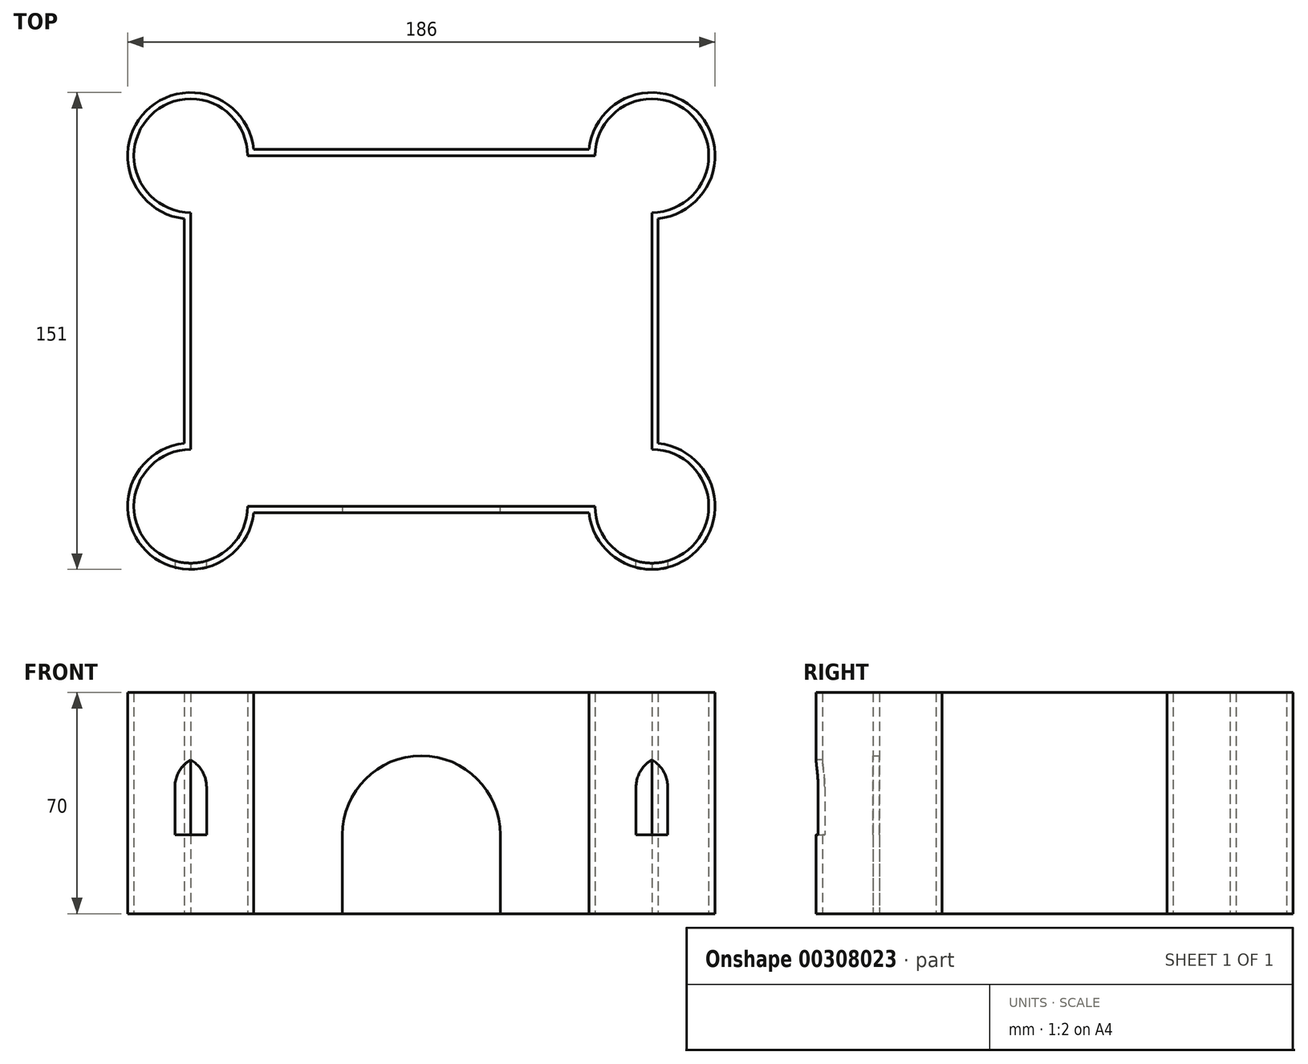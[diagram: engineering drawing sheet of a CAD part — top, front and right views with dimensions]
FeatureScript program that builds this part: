
annotation { "Feature Type Name" : "Feature", "Feature Type Description" : "" }
export const myFeature = defineFeature(function(context is Context, id is Id, definition is map)
    precondition{}
    {
        {
            var Q0;
            Q0=qCreatedBy(makeId("Top.planeOp"),FACE);
            var sketch = newSketch(context, id + "F0", { "sketchPlane" : qUnion([Q0])});
            skLineSegment(sketch, "E0.top", {"start": v(-53.1, 57.5) * mm, "end": v(53.1, 57.5) * mm});
            skLineSegment(sketch, "E0.left", {"start": v(-75, -35.6) * mm, "end": v(-75, 35.6) * mm});
            skPoint(sketch, "E0.middle", {"position": v(0, 0) * mm});
            skLineSegment(sketch, "E1.bottom", {"start": v(55, -55.5) * mm, "end": v(-55, -55.5) * mm});
            skLineSegment(sketch, "E1.top", {"start": v(55, 55.5) * mm, "end": v(-55, 55.5) * mm});
            skLineSegment(sketch, "E1.left", {"start": v(73, -37.5) * mm, "end": v(73, 37.5) * mm});
            skLineSegment(sketch, "E1.right", {"start": v(-73, -37.5) * mm, "end": v(-73, 37.5) * mm});
            skArc(sketch, "E2", {"start": v(-75, -35.6) * mm, "mid": v(-87.14, -69.64) * mm, "end": v(-53.1, -57.5) * mm});
            skArc(sketch, "E3", {"start": v(-73, -37.5) * mm, "mid": v(-85.73, -68.23) * mm, "end": v(-55, -55.5) * mm});
            skArc(sketch, "E4.MirrorC", {"start": v(75, -35.6) * mm, "mid": v(87.14, -69.64) * mm, "end": v(53.1, -57.5) * mm});
            skArc(sketch, "E5.MirrorC", {"start": v(73, -37.5) * mm, "mid": v(85.73, -68.23) * mm, "end": v(55, -55.5) * mm});
            skArc(sketch, "E6.MirrorC", {"start": v(-75, 35.6) * mm, "mid": v(-87.14, 69.64) * mm, "end": v(-53.1, 57.5) * mm});
            skArc(sketch, "E7.MirrorC", {"start": v(-73, 37.5) * mm, "mid": v(-85.73, 68.23) * mm, "end": v(-55, 55.5) * mm});
            skArc(sketch, "E8.MirrorC", {"start": v(73, 37.5) * mm, "mid": v(85.73, 68.23) * mm, "end": v(55, 55.5) * mm});
            skArc(sketch, "E9.MirrorC", {"start": v(75, 35.6) * mm, "mid": v(87.14, 69.64) * mm, "end": v(53.1, 57.5) * mm});
            skPoint(sketch, "E10.orphan", {"position": v(-75, 57.5) * mm});
            skPoint(sketch, "E11.trimOffspring.end.orphan", {"position": v(75, 57.5) * mm});
            skLineSegment(sketch, "E12.trimOffspring", {"start": v(75, -35.6) * mm, "end": v(75, 35.6) * mm});
            skPoint(sketch, "E13.orphan", {"position": v(75, -57.5) * mm});
            skLineSegment(sketch, "E14.trimOffspring", {"start": v(-53.1, -57.5) * mm, "end": v(53.1, -57.5) * mm});
            skPoint(sketch, "E15.orphan", {"position": v(-75, -57.5) * mm});
            skLineSegment(sketch, "E16", {"start": v(25, -57.5) * mm, "end": v(25, -55.5) * mm});
            skLineSegment(sketch, "E17", {"start": v(25, -55.5) * mm, "end": v(-25, -55.5) * mm});
            skLineSegment(sketch, "E18", {"start": v(-25, -55.5) * mm, "end": v(-25, -57.5) * mm});
            skLineSegment(sketch, "E19", {"start": v(-73, -55.5) * mm, "end": v(-73, -73.5) * mm});
            skLineSegment(sketch, "E20", {"start": v(-68, -74.86) * mm, "end": v(-68, -72.8) * mm});
            skLineSegment(sketch, "E21", {"start": v(-78, -72.8) * mm, "end": v(-78, -74.86) * mm});
            skLineSegment(sketch, "E22.MirrorCS", {"start": v(78, -72.8) * mm, "end": v(78, -74.86) * mm});
            skLineSegment(sketch, "E23.MirrorCS", {"start": v(68, -74.86) * mm, "end": v(68, -72.8) * mm});
            skSolve(sketch);
        }
        {
            var Q0;
            Q0 = qSketchRegion(id + "F0", true);
            extrude(context, id + "F1", {"entities" : qUnion([Q0]), "depth" : 70 * mm});
        }
        {
            var Q0;
            {var subQ0=sQuery(id+"F0.wireOp",EDGE,"E16");Q0=makeQuery(id+"F0.imprint","IMPRINT",FACE,{"disambiguationData":[TD([[makeQuery(id+"F0.imprint","IMPRINT",EDGE,{"derivedFrom":subQ0}),1.0]])]});}
            var Q1;
            {var subQ0=sQuery(id+"F0.wireOp",EDGE,"E20");Q1=makeQuery(id+"F0.imprint","IMPRINT",FACE,{"disambiguationData":[TD([[makeQuery(id+"F0.imprint","IMPRINT",EDGE,{"derivedFrom":subQ0}),1.0]])]});}
            var Q2;
            {var subQ0=sQuery(id+"F0.wireOp",EDGE,"E22.MirrorCS");Q2=makeQuery(id+"F0.imprint","IMPRINT",FACE,{"disambiguationData":[TD([[makeQuery(id+"F0.imprint","IMPRINT",EDGE,{"derivedFrom":subQ0}),-1.0]])]});}
            extrude(context, id + "F2", {"entities" : qUnion([Q0, Q1, Q2]), "operationType" : NewBodyOperationType.REMOVE, "depth" : 50 * mm});
        }
        {
            var Q0;
            Q0=makeQuery(id+"F2.boolean.opBoolean","COPY",EDGE,{"derivedFrom":makeQuery(id+"F2.opExtrude","CAP_EDGE",EDGE,{"disambiguationData":[OSD([sQuery(id+"F0.wireOp",EDGE,"E16")])],"isStart":false})});
            var Q1;
            Q1=makeQuery(id+"F2.boolean.opBoolean","COPY",EDGE,{"derivedFrom":makeQuery(id+"F2.opExtrude","CAP_EDGE",EDGE,{"disambiguationData":[OSD([sQuery(id+"F0.wireOp",EDGE,"E18")])],"isStart":false})});
            fillet(context, id + "F3", {"entities" : qUnion([Q0, Q1]), "radius" : 25 * mm, "tangentPropagation" : true, "allowEdgeOverflow" : false});
        }
        {
            var Q0;
            {var subQ2=sQuery(id+"F0.wireOp",EDGE,"E20");Q0=makeQuery(id+"F0.imprint","IMPRINT",FACE,{"disambiguationData":[TD([[makeQuery(id+"F0.imprint","IMPRINT",EDGE,{"derivedFrom":subQ2}),1.0]])]});}
            var Q1;
            {var subQ0=sQuery(id+"F0.wireOp",EDGE,"E22.MirrorCS");Q1=makeQuery(id+"F0.imprint","IMPRINT",FACE,{"disambiguationData":[TD([[makeQuery(id+"F0.imprint","IMPRINT",EDGE,{"derivedFrom":subQ0}),-1.0]])]});}
            extrude(context, id + "F4", {"entities" : qUnion([Q0, Q1]), "operationType" : NewBodyOperationType.ADD, "depth" : 25 * mm});
        }
        {
            var Q0;
            Q0=makeQuery(id+"F2.boolean.opBoolean","COPY",EDGE,{"derivedFrom":makeQuery(id+"F2.opExtrude","CAP_EDGE",EDGE,{"disambiguationData":[OSD([sQuery(id+"F0.wireOp",EDGE,"E21")])],"isStart":false})});
            var Q1;
            Q1=makeQuery(id+"F2.boolean.opBoolean","COPY",EDGE,{"derivedFrom":makeQuery(id+"F2.opExtrude","CAP_EDGE",EDGE,{"disambiguationData":[OSD([sQuery(id+"F0.wireOp",EDGE,"E20")])],"isStart":false})});
            var Q2;
            Q2=makeQuery(id+"F2.boolean.opBoolean","COPY",EDGE,{"derivedFrom":makeQuery(id+"F2.opExtrude","CAP_EDGE",EDGE,{"disambiguationData":[OSD([sQuery(id+"F0.wireOp",EDGE,"E23.MirrorCS")])],"isStart":false})});
            var Q3;
            Q3=makeQuery(id+"F2.boolean.opBoolean","COPY",EDGE,{"derivedFrom":makeQuery(id+"F2.opExtrude","CAP_EDGE",EDGE,{"disambiguationData":[OSD([sQuery(id+"F0.wireOp",EDGE,"E22.MirrorCS")])],"isStart":false})});
            fillet(context, id + "F5", {"entities" : qUnion([Q0, Q1, Q2, Q3]), "radius" : 9.9 * mm, "tangentPropagation" : true, "allowEdgeOverflow" : false});
        }
    });
